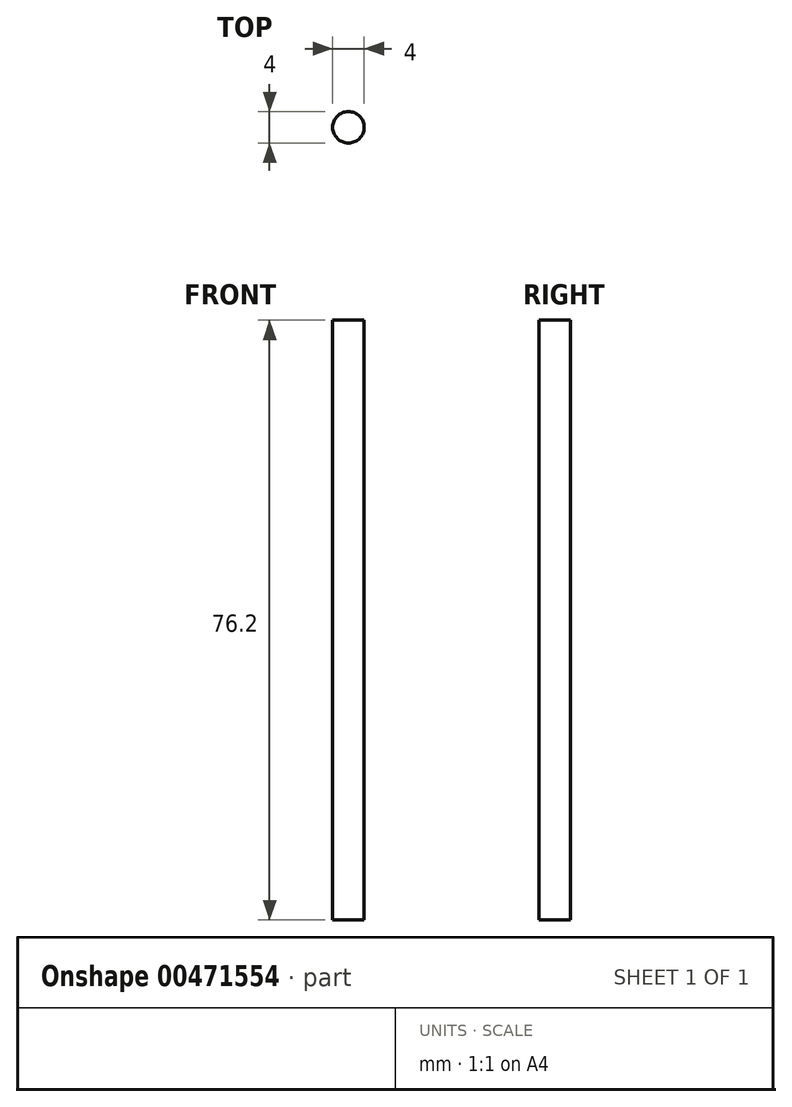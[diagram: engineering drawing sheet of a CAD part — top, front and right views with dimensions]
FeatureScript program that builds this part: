
annotation { "Feature Type Name" : "Feature", "Feature Type Description" : "" }
export const myFeature = defineFeature(function(context is Context, id is Id, definition is map)
    precondition{}
    {
        {
            var Q0;
            Q0=qCreatedBy(makeId("Top.planeOp"),FACE);
            var sketch = newSketch(context, id + "F0", { "sketchPlane" : qUnion([Q0])});
            skCircle(sketch, "E0", {"center": v(0, 0) * mm, "radius": 26.36 * mm});
            skSolve(sketch);
        }
        {
            var Q0;
            Q0=makeQuery(id+"F0.imprint","IMPRINT",FACE,{"disambiguationData":[TD([[makeQuery(id+"F0.imprint","IMPRINT",EDGE,{"derivedFrom":sQuery(id+"F0.wireOp",EDGE,"E0")}),1.0]])]});
            extrude(context, id + "F1", {"entities" : qUnion([Q0]), "depth" : 100 * mm});
        }
        {
            var Q0;
            Q0=makeQuery(id+"F1.opExtrude","SWEPT_BODY",BODY,{"disambiguationData":[OSD([sQuery(id+"F0.wireOp",EDGE,"E0")])]});
            deleteBodies(context, id + "F2", {"entities" : qUnion([Q0])});
        }
        {
            var Q0;
            Q0=qCreatedBy(makeId("Top.planeOp"),FACE);
            var sketch = newSketch(context, id + "F3", { "sketchPlane" : qUnion([Q0])});
            skCircle(sketch, "E1", {"center": v(0, 0) * mm, "radius": 2 * mm});
            skSolve(sketch);
        }
        {
            var Q0;
            Q0=makeQuery(id+"F3.imprint","IMPRINT",FACE,{"disambiguationData":[TD([[makeQuery(id+"F3.imprint","IMPRINT",EDGE,{"derivedFrom":sQuery(id+"F3.wireOp",EDGE,"E1")}),1.0]])]});
            extrude(context, id + "F4", {"entities" : qUnion([Q0]), "depth" : 76.2 * mm});
        }
    });
